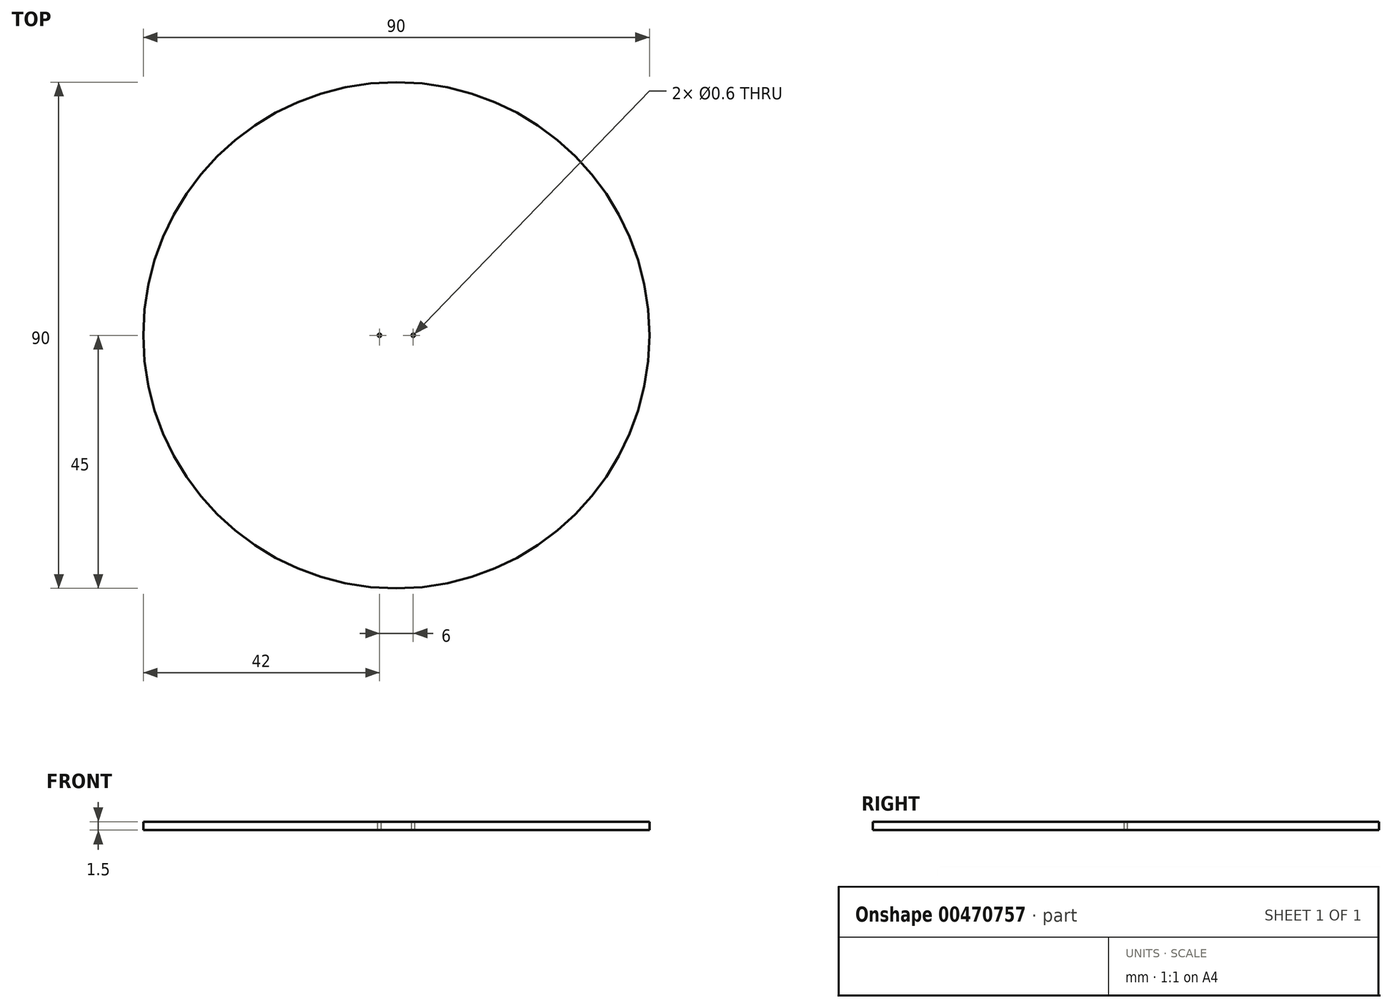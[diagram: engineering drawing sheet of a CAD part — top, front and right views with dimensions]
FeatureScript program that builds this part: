
annotation { "Feature Type Name" : "Feature", "Feature Type Description" : "" }
export const myFeature = defineFeature(function(context is Context, id is Id, definition is map)
    precondition{}
    {
        {
            var Q0;
            Q0=qCreatedBy(makeId("Top.planeOp"),FACE);
            var sketch = newSketch(context, id + "F0", { "sketchPlane" : qUnion([Q0])});
            skCircle(sketch, "E0", {"center": v(0, 0) * mm, "radius": 45 * mm});
            skSolve(sketch);
        }
        {
            var Q0;
            Q0=makeQuery(id+"F0.imprint","IMPRINT",FACE,{"disambiguationData":[TD([[makeQuery(id+"F0.imprint","IMPRINT",EDGE,{"derivedFrom":sQuery(id+"F0.wireOp",EDGE,"E0")}),1.0]])]});
            extrude(context, id + "F1", {"entities" : qUnion([Q0]), "depth" : 1.5 * mm});
        }
        {
            var Q0;
            Q0=qCreatedBy(makeId("Top.planeOp"),FACE);
            var sketch = newSketch(context, id + "F2", { "sketchPlane" : qUnion([Q0])});
            skLineSegment(sketch, "E1", {"start": v(0, 0) * mm, "end": v(-3, 0) * mm, "construction": true});
            skLineSegment(sketch, "E2", {"start": v(0, 0) * mm, "end": v(3, 0) * mm, "construction": true});
            skSolve(sketch);
        }
        {
            var Q0;
            Q0=sQuery(id+"F2.wireOp",VERTEX,"E1.end");
            var Q1;
            Q1=sQuery(id+"F2.wireOp",VERTEX,"E2.end");
            var Q2;
            Q2=makeQuery(id+"F1.opExtrude","SWEPT_BODY",BODY,{"disambiguationData":[OSD([sQuery(id+"F0.wireOp",EDGE,"E0")])]});
            hole(context, id + "F3", {"style" : HoleStyle.SIMPLE, "endStyle" : HoleEndStyle.THROUGH, "oppositeDirection" : true, "holeDiameter" : .6 * mm, "isTappedThrough" : true, "tappedDepth" : 12 * mm, "tapClearance" : 3, "locations" : qUnion([Q0, Q1]), "scope" : qUnion([Q2]), "startStyle" : HoleStartStyle.PART});
        }
    });
